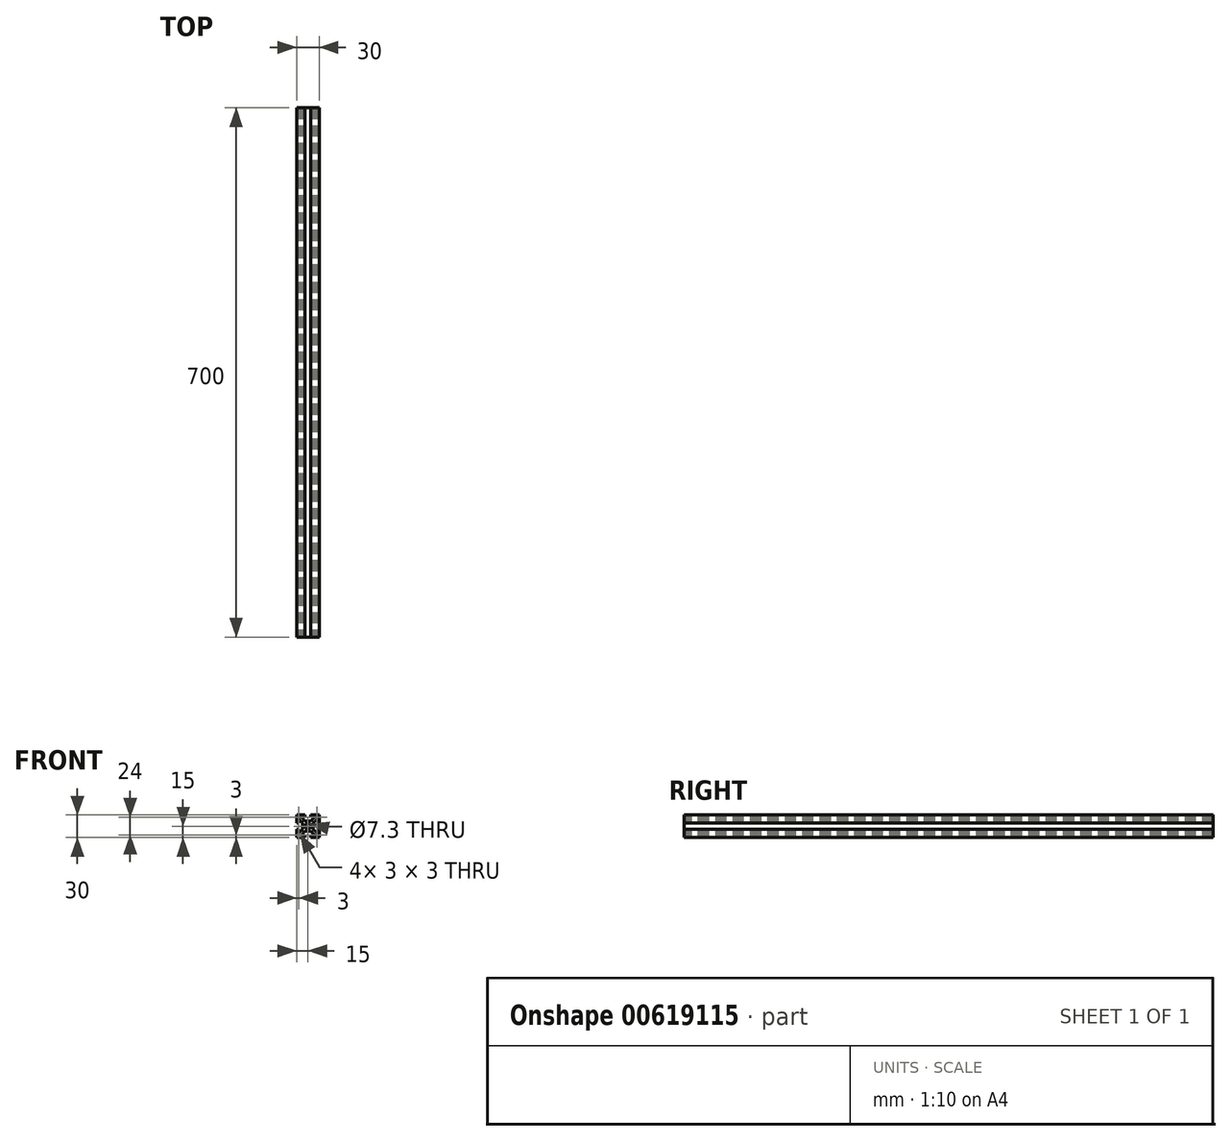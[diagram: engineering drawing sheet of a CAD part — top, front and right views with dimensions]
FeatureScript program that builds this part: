
annotation { "Feature Type Name" : "Feature", "Feature Type Description" : "" }
export const myFeature = defineFeature(function(context is Context, id is Id, definition is map)
    precondition{}
    {
        {
            var Q0;
            Q0=qCreatedBy(makeId("Front.planeOp"),FACE);
            var sketch = newSketch(context, id + "F0", { "sketchPlane" : qUnion([Q0])});
            skLineSegment(sketch, "E0.bottom", {"start": v(-15, 15) * mm, "end": v(15, 15) * mm});
            skLineSegment(sketch, "E0.top", {"start": v(-15, -15) * mm, "end": v(15, -15) * mm});
            skLineSegment(sketch, "E0.left", {"start": v(-15, 15) * mm, "end": v(-15, -15) * mm});
            skLineSegment(sketch, "E0.right", {"start": v(15, 15) * mm, "end": v(15, -15) * mm});
            skPoint(sketch, "E0.middle", {"position": v(0, 0) * mm});
            skSolve(sketch);
        }
        {
            var Q0;
            Q0 = qSketchRegion(id + "F0", true);
            extrude(context, id + "F1", {"entities" : qUnion([Q0]), "depth" : 700 * mm, "offsetDistance" : 25 * mm});
        }
        {
            var Q0;
            Q0=makeQuery(id+"F1.opExtrude","CAP_FACE",FACE,{"disambiguationData":[OSD([sQuery(id+"F0.wireOp",EDGE,"E0.bottom"),sQuery(id+"F0.wireOp",EDGE,"E0.top"),sQuery(id+"F0.wireOp",EDGE,"E0.left"),sQuery(id+"F0.wireOp",EDGE,"E0.right")])],"isStart":false});
            var sketch = newSketch(context, id + "F2", { "sketchPlane" : qUnion([Q0])});
            skLineSegment(sketch, "E1", {"start": v(-15, 4) * mm, "end": v(-13, 4) * mm});
            skLineSegment(sketch, "E2", {"start": v(-13, 4) * mm, "end": v(-13, 8) * mm});
            skLineSegment(sketch, "E3", {"start": v(-13, 8) * mm, "end": v(-11, 8) * mm});
            skLineSegment(sketch, "E4", {"start": v(-11, 8) * mm, "end": v(-7, 4) * mm});
            skLineSegment(sketch, "E5", {"start": v(-7, 4) * mm, "end": v(-7, -4) * mm});
            skLineSegment(sketch, "E6", {"start": v(-7, -4) * mm, "end": v(-11, -8) * mm});
            skLineSegment(sketch, "E7", {"start": v(-11, -8) * mm, "end": v(-13, -8) * mm});
            skLineSegment(sketch, "E8", {"start": v(-13, -8) * mm, "end": v(-13, -4) * mm});
            skLineSegment(sketch, "E9", {"start": v(-13, -4) * mm, "end": v(-15, -4) * mm});
            skLineSegment(sketch, "E10", {"start": v(-15, -4) * mm, "end": v(-15, 4) * mm});
            skLineSegment(sketch, "E11", {"start": v(-4, 15) * mm, "end": v(4, 15) * mm});
            skLineSegment(sketch, "E12", {"start": v(4, 15) * mm, "end": v(4, 13) * mm});
            skLineSegment(sketch, "E13", {"start": v(4, 13) * mm, "end": v(8, 13) * mm});
            skLineSegment(sketch, "E14", {"start": v(8, 13) * mm, "end": v(8, 11) * mm});
            skLineSegment(sketch, "E15", {"start": v(8, 11) * mm, "end": v(4, 7) * mm});
            skLineSegment(sketch, "E16", {"start": v(4, 7) * mm, "end": v(-4, 7) * mm});
            skLineSegment(sketch, "E17", {"start": v(-4, 7) * mm, "end": v(-8, 11) * mm});
            skLineSegment(sketch, "E18", {"start": v(-8, 11) * mm, "end": v(-8, 13) * mm});
            skLineSegment(sketch, "E19", {"start": v(-8, 13) * mm, "end": v(-4, 13) * mm});
            skLineSegment(sketch, "E20", {"start": v(-4, 13) * mm, "end": v(-4, 15) * mm});
            skLineSegment(sketch, "E21", {"start": v(15, -4) * mm, "end": v(15, 4) * mm});
            skLineSegment(sketch, "E22", {"start": v(15, 4) * mm, "end": v(13, 4) * mm});
            skLineSegment(sketch, "E23", {"start": v(13, 4) * mm, "end": v(13, 8) * mm});
            skLineSegment(sketch, "E24", {"start": v(13, 8) * mm, "end": v(11, 8) * mm});
            skLineSegment(sketch, "E25", {"start": v(11, 8) * mm, "end": v(7, 4) * mm});
            skLineSegment(sketch, "E26", {"start": v(7, 4) * mm, "end": v(7, -4) * mm});
            skLineSegment(sketch, "E27", {"start": v(7, -4) * mm, "end": v(11, -8) * mm});
            skLineSegment(sketch, "E28", {"start": v(11, -8) * mm, "end": v(13, -8) * mm});
            skLineSegment(sketch, "E29", {"start": v(13, -8) * mm, "end": v(13, -4) * mm});
            skLineSegment(sketch, "E30", {"start": v(13, -4) * mm, "end": v(15, -4) * mm});
            skCircle(sketch, "E31", {"center": v(0, 0) * mm, "radius": 3.65 * mm});
            skLineSegment(sketch, "E32", {"start": v(-4, -15) * mm, "end": v(4, -15) * mm});
            skPoint(sketch, "E32.endSnap0", {"position": v(4, 14) * mm});
            skLineSegment(sketch, "E33", {"start": v(4, -15) * mm, "end": v(3.95, -12.94) * mm});
            skLineSegment(sketch, "E34", {"start": v(3.95, -12.94) * mm, "end": v(8, -12.94) * mm});
            skLineSegment(sketch, "E35", {"start": v(8, -12.94) * mm, "end": v(8, -10.94) * mm});
            skLineSegment(sketch, "E36", {"start": v(8, -10.94) * mm, "end": v(4, -6.94) * mm});
            skLineSegment(sketch, "E37", {"start": v(4, -6.94) * mm, "end": v(-4, -6.94) * mm});
            skLineSegment(sketch, "E38", {"start": v(-4, -6.94) * mm, "end": v(-8, -10.94) * mm});
            skLineSegment(sketch, "E39", {"start": v(-8, -10.94) * mm, "end": v(-8, -12.94) * mm});
            skLineSegment(sketch, "E40", {"start": v(-8, -12.94) * mm, "end": v(-4, -12.94) * mm});
            skLineSegment(sketch, "E41", {"start": v(-4, -12.94) * mm, "end": v(-4, -15) * mm});
            skLineSegment(sketch, "E42.bottom", {"start": v(10.5, 13.5) * mm, "end": v(13.5, 13.5) * mm});
            skLineSegment(sketch, "E42.top", {"start": v(10.5, 10.5) * mm, "end": v(13.5, 10.5) * mm});
            skLineSegment(sketch, "E42.left", {"start": v(10.5, 13.5) * mm, "end": v(10.5, 10.5) * mm});
            skLineSegment(sketch, "E42.right", {"start": v(13.5, 13.5) * mm, "end": v(13.5, 10.5) * mm});
            skPoint(sketch, "E42.middle", {"position": v(12, 12) * mm});
            skLineSegment(sketch, "E43.bottom", {"start": v(-13.5, 13.5) * mm, "end": v(-10.5, 13.5) * mm});
            skLineSegment(sketch, "E43.top", {"start": v(-13.5, 10.5) * mm, "end": v(-10.5, 10.5) * mm});
            skLineSegment(sketch, "E43.left", {"start": v(-13.5, 13.5) * mm, "end": v(-13.5, 10.5) * mm});
            skLineSegment(sketch, "E43.right", {"start": v(-10.5, 13.5) * mm, "end": v(-10.5, 10.5) * mm});
            skPoint(sketch, "E43.middle", {"position": v(-12, 12) * mm});
            skLineSegment(sketch, "E44.bottom", {"start": v(13.5, -13.5) * mm, "end": v(10.5, -13.5) * mm});
            skLineSegment(sketch, "E44.top", {"start": v(13.5, -10.5) * mm, "end": v(10.5, -10.5) * mm});
            skLineSegment(sketch, "E44.left", {"start": v(13.5, -13.5) * mm, "end": v(13.5, -10.5) * mm});
            skLineSegment(sketch, "E44.right", {"start": v(10.5, -13.5) * mm, "end": v(10.5, -10.5) * mm});
            skPoint(sketch, "E44.middle", {"position": v(12, -12) * mm});
            skLineSegment(sketch, "E45.bottom", {"start": v(-13.5, -13.5) * mm, "end": v(-10.5, -13.5) * mm});
            skLineSegment(sketch, "E45.top", {"start": v(-13.5, -10.5) * mm, "end": v(-10.5, -10.5) * mm});
            skLineSegment(sketch, "E45.left", {"start": v(-13.5, -13.5) * mm, "end": v(-13.5, -10.5) * mm});
            skLineSegment(sketch, "E45.right", {"start": v(-10.5, -13.5) * mm, "end": v(-10.5, -10.5) * mm});
            skPoint(sketch, "E45.middle", {"position": v(-12, -12) * mm});
            skSolve(sketch);
        }
        {
            var Q0;
            Q0 = qSketchRegion(id + "F2", true);
            extrude(context, id + "F3", {"entities" : qUnion([Q0]), "operationType" : NewBodyOperationType.REMOVE, "endBound" : BoundingType.THROUGH_ALL, "oppositeDirection" : true, "depth" : 25 * mm, "offsetDistance" : 25 * mm});
        }
    });
